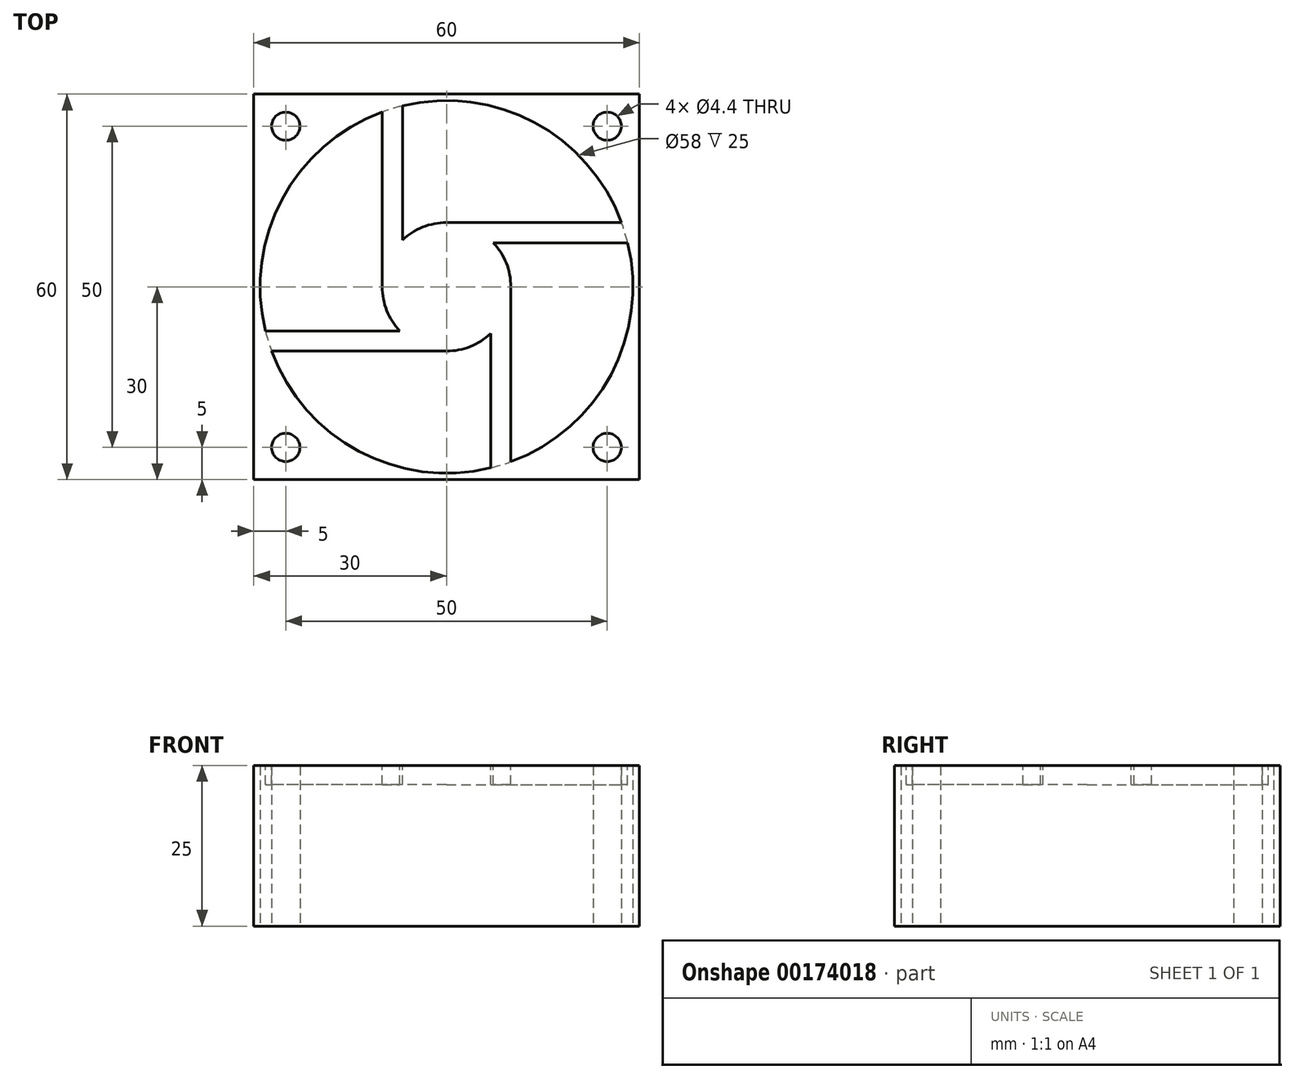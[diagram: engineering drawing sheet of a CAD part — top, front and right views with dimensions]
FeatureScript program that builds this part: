
annotation { "Feature Type Name" : "Feature", "Feature Type Description" : "" }
export const myFeature = defineFeature(function(context is Context, id is Id, definition is map)
    precondition{}
    {
        {
            var Q0;
            Q0=qCreatedBy(makeId("Top.planeOp"),FACE);
            var sketch = newSketch(context, id + "F0", { "sketchPlane" : qUnion([Q0])});
            skLineSegment(sketch, "E0.bottom", {"start": v(30, -30) * mm, "end": v(-30, -30) * mm});
            skLineSegment(sketch, "E0.top", {"start": v(30, 30) * mm, "end": v(-30, 30) * mm});
            skLineSegment(sketch, "E0.left", {"start": v(30, -30) * mm, "end": v(30, 30) * mm});
            skLineSegment(sketch, "E0.right", {"start": v(-30, -30) * mm, "end": v(-30, 30) * mm});
            skPoint(sketch, "E0.middle", {"position": v(0, 0) * mm});
            skLineSegment(sketch, "E1.bottom", {"start": v(25, 25) * mm, "end": v(-25, 25) * mm, "construction": true});
            skLineSegment(sketch, "E1.top", {"start": v(25, -25) * mm, "end": v(-25, -25) * mm, "construction": true});
            skLineSegment(sketch, "E1.left", {"start": v(25, 25) * mm, "end": v(25, -25) * mm, "construction": true});
            skLineSegment(sketch, "E1.right", {"start": v(-25, 25) * mm, "end": v(-25, -25) * mm, "construction": true});
            skCircle(sketch, "E2", {"center": v(-25, 25) * mm, "radius": 2.2 * mm});
            skCircle(sketch, "E3", {"center": v(25, 25) * mm, "radius": 2.2 * mm});
            skCircle(sketch, "E4", {"center": v(25, -25) * mm, "radius": 2.2 * mm});
            skCircle(sketch, "E5", {"center": v(-25, -25) * mm, "radius": 2.2 * mm});
            skCircle(sketch, "E6", {"center": v(0, 0) * mm, "radius": 29 * mm});
            skSolve(sketch);
        }
        {
            var Q0;
            Q0 = qSketchRegion(id + "F0", true);
            extrude(context, id + "F1", {"entities" : qUnion([Q0]), "depth" : 25 * mm});
        }
        {
            var Q0;
            Q0=makeQuery(id+"F1.opExtrude","CAP_FACE",FACE,{"disambiguationData":[OSD([sQuery(id+"F0.wireOp",EDGE,"E0.bottom"),sQuery(id+"F0.wireOp",EDGE,"E0.top"),sQuery(id+"F0.wireOp",EDGE,"E0.left"),sQuery(id+"F0.wireOp",EDGE,"E0.right"),sQuery(id+"F0.wireOp",EDGE,"E2"),sQuery(id+"F0.wireOp",EDGE,"E3"),sQuery(id+"F0.wireOp",EDGE,"E4"),sQuery(id+"F0.wireOp",EDGE,"E5"),sQuery(id+"F0.wireOp",EDGE,"E6")])],"isStart":false});
            var sketch = newSketch(context, id + "F2", { "sketchPlane" : qUnion([Q0])});
            skArc(sketch, "E7", {"start": v(-10, 0) * mm, "mid": v(-9.3, -3.7) * mm, "end": v(-7.27, -6.86) * mm});
            skLineSegment(sketch, "E8", {"start": v(0, 10) * mm, "end": v(27.22, 10) * mm});
            skLineSegment(sketch, "E9", {"start": v(7.27, 6.86) * mm, "end": v(28.18, 6.86) * mm});
            skLineSegment(sketch, "E10.1.0", {"start": v(-10, 0) * mm, "end": v(-10, 27.22) * mm});
            skLineSegment(sketch, "E10.1.1", {"start": v(-6.86, 7.27) * mm, "end": v(-6.86, 28.18) * mm});
            skLineSegment(sketch, "E10.2.0", {"start": v(0, -10) * mm, "end": v(-27.22, -10) * mm});
            skLineSegment(sketch, "E10.2.1", {"start": v(-7.27, -6.86) * mm, "end": v(-28.18, -6.86) * mm});
            skLineSegment(sketch, "E10.3.0", {"start": v(10, 0) * mm, "end": v(10, -27.22) * mm});
            skLineSegment(sketch, "E10.3.1", {"start": v(6.86, -7.27) * mm, "end": v(6.86, -28.18) * mm});
            skArc(sketch, "E11.trimOffspring", {"start": v(0, -10) * mm, "mid": v(3.7, -9.3) * mm, "end": v(6.86, -7.27) * mm});
            skArc(sketch, "E12.trimOffspring", {"start": v(10, 0) * mm, "mid": v(9.3, 3.7) * mm, "end": v(7.27, 6.86) * mm});
            skArc(sketch, "E13.trimOffspring", {"start": v(0, 10) * mm, "mid": v(-3.7, 9.3) * mm, "end": v(-6.86, 7.27) * mm});
            skArc(sketch, "E14.0", {"start": v(-28.18, -6.86) * mm, "mid": v(-27.74, -8.45) * mm, "end": v(-27.22, -10) * mm});
            skArc(sketch, "E15.trimOffspring", {"start": v(-6.86, 28.18) * mm, "mid": v(-8.45, 27.74) * mm, "end": v(-10, 27.22) * mm});
            skArc(sketch, "E16.trimOffspring", {"start": v(28.18, 6.86) * mm, "mid": v(27.74, 8.45) * mm, "end": v(27.22, 10) * mm});
            skArc(sketch, "E17.trimOffspring", {"start": v(6.86, -28.18) * mm, "mid": v(8.45, -27.74) * mm, "end": v(10, -27.22) * mm});
            skSolve(sketch);
        }
        {
            var Q0;
            Q0 = qSketchRegion(id + "F2", true);
            extrude(context, id + "F3", {"entities" : qUnion([Q0]), "operationType" : NewBodyOperationType.ADD, "oppositeDirection" : true, "depth" : 3 * mm});
        }
    });
